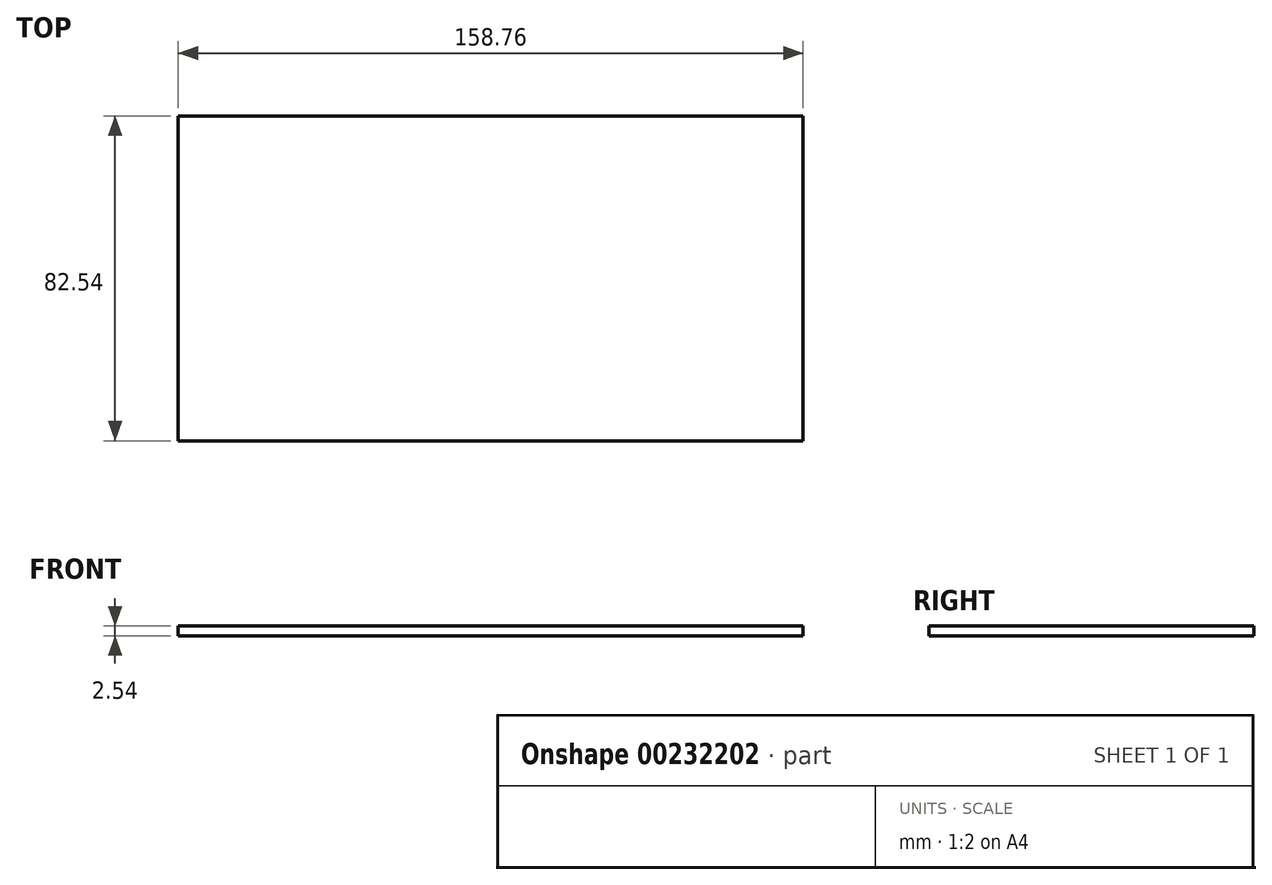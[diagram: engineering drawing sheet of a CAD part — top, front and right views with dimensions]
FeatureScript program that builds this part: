
annotation { "Feature Type Name" : "Feature", "Feature Type Description" : "" }
export const myFeature = defineFeature(function(context is Context, id is Id, definition is map)
    precondition{}
    {
        {
            var Q0;
            Q0=qCreatedBy(makeId("Top.planeOp"),FACE);
            var sketch = newSketch(context, id + "F0", { "sketchPlane" : qUnion([Q0])});
            skLineSegment(sketch, "E0.bottom", {"start": v(76.2, 38.1) * mm, "end": v(-76.2, 38.1) * mm});
            skLineSegment(sketch, "E0.top", {"start": v(76.2, -38.1) * mm, "end": v(-76.2, -38.1) * mm});
            skLineSegment(sketch, "E0.left", {"start": v(76.2, 38.1) * mm, "end": v(76.2, -38.1) * mm});
            skLineSegment(sketch, "E0.right", {"start": v(-76.2, 38.1) * mm, "end": v(-76.2, -38.1) * mm});
            skPoint(sketch, "E0.middle", {"position": v(0, 0) * mm});
            skLineSegment(sketch, "E1.bottom", {"start": v(63.5, 25.4) * mm, "end": v(-63.5, 25.4) * mm});
            skLineSegment(sketch, "E1.top", {"start": v(63.5, -25.4) * mm, "end": v(-63.5, -25.4) * mm});
            skLineSegment(sketch, "E1.left", {"start": v(63.5, 25.4) * mm, "end": v(63.5, -25.4) * mm});
            skLineSegment(sketch, "E1.right", {"start": v(-63.5, 25.4) * mm, "end": v(-63.5, -25.4) * mm});
            skLineSegment(sketch, "E2.bottom", {"start": v(79.38, 41.28) * mm, "end": v(-79.37, 41.27) * mm});
            skLineSegment(sketch, "E2.top", {"start": v(79.38, -41.27) * mm, "end": v(-79.37, -41.28) * mm});
            skLineSegment(sketch, "E2.left", {"start": v(79.38, 41.28) * mm, "end": v(79.38, -41.27) * mm});
            skLineSegment(sketch, "E2.right", {"start": v(-79.38, 41.27) * mm, "end": v(-79.37, -41.28) * mm});
            skSolve(sketch);
        }
        {
            var Q0;
            Q0=makeQuery(id+"F0.imprint","IMPRINT",FACE,{"disambiguationData":[TD([[makeQuery(id+"F0.imprint","IMPRINT",EDGE,{"derivedFrom":sQuery(id+"F0.wireOp",EDGE,"E0.bottom")}),1.0]])]});
            var Q1;
            Q1=makeQuery(id+"F0.imprint","IMPRINT",FACE,{"disambiguationData":[TD([[makeQuery(id+"F0.imprint","IMPRINT",EDGE,{"derivedFrom":sQuery(id+"F0.wireOp",EDGE,"E1.bottom")}),1.0]])]});
            var Q2;
            Q2 = qSketchRegion(id + "F0", true);
            extrude(context, id + "F1", {"entities" : qUnion([Q0, Q1, Q2]), "depth" : 2.54 * mm});
        }
    });
